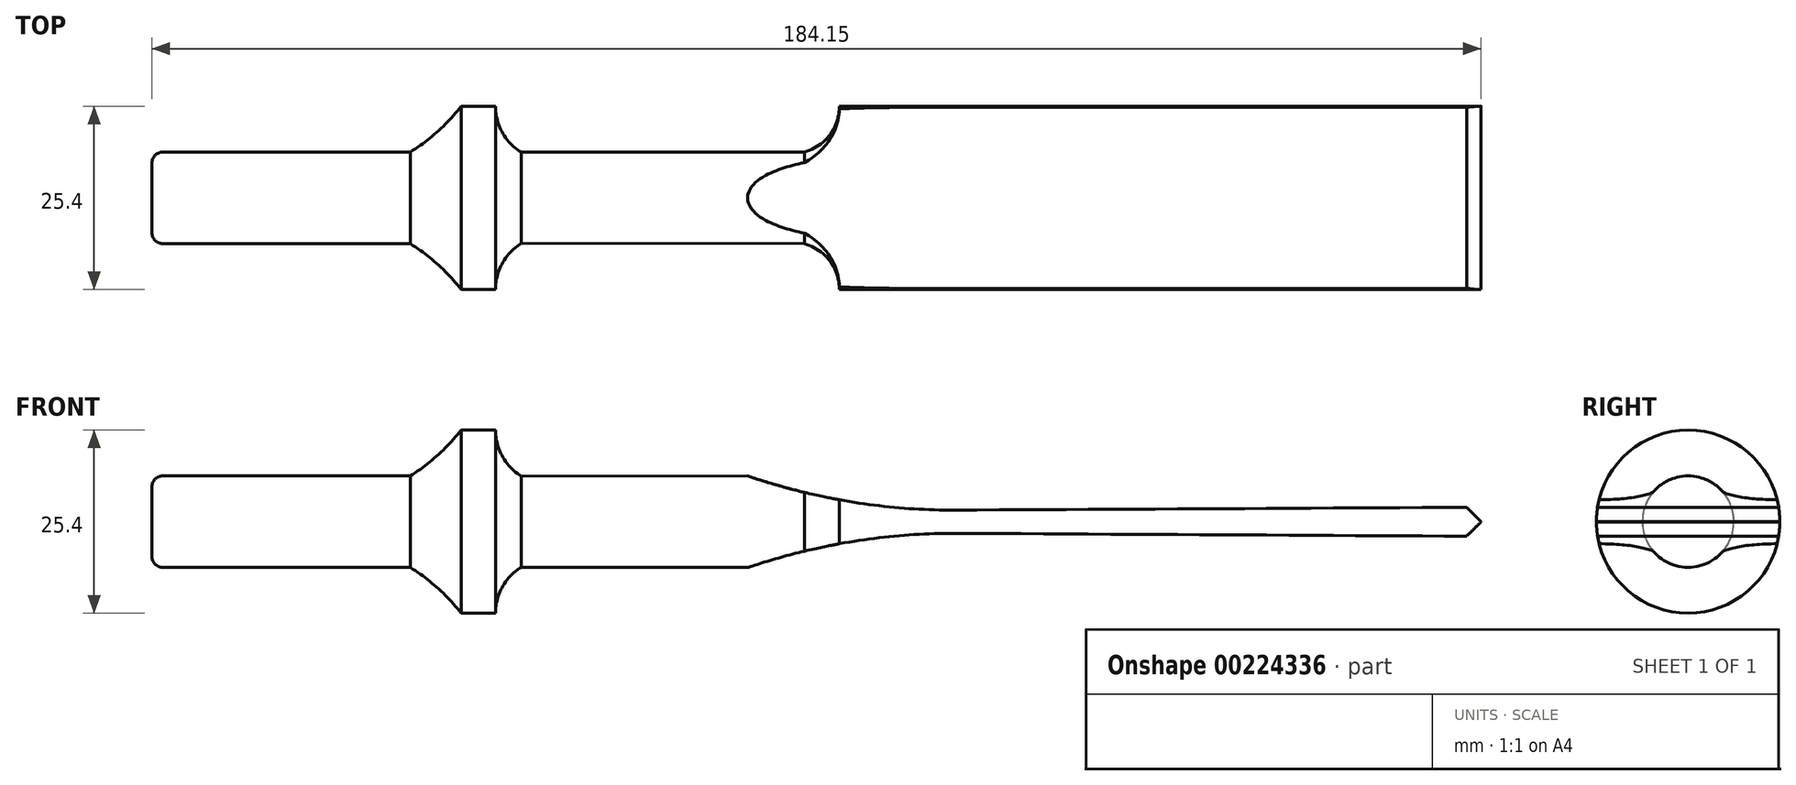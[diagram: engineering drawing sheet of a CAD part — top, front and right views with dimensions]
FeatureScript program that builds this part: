
annotation { "Feature Type Name" : "Feature", "Feature Type Description" : "" }
export const myFeature = defineFeature(function(context is Context, id is Id, definition is map)
    precondition{}
    {
        {
            var Q0;
            Q0=qCreatedBy(makeId("Front.planeOp"),FACE);
            var sketch = newSketch(context, id + "F0", { "sketchPlane" : qUnion([Q0])});
            skLineSegment(sketch, "E0", {"start": v(-87.11, -21.44) * mm, "end": v(95.51, -21.44) * mm});
            skLineSegment(sketch, "E1", {"start": v(95.51, -21.44) * mm, "end": v(95.51, -8.74) * mm});
            skLineSegment(sketch, "E2", {"start": v(-88.64, -19.91) * mm, "end": v(-88.64, -16.61) * mm});
            skLineSegment(sketch, "E3", {"start": v(-87.11, -15.09) * mm, "end": v(-52.84, -15.09) * mm});
            skLineSegment(sketch, "E4", {"start": v(95.51, -8.74) * mm, "end": v(6.61, -8.74) * mm});
            skLineSegment(sketch, "E5", {"start": v(-45.79, -8.74) * mm, "end": v(-41.04, -8.74) * mm});
            skLineSegment(sketch, "E6", {"start": v(-37.44, -15.12) * mm, "end": v(1.76, -15.1) * mm});
            skArc(sketch, "E7", {"start": v(-1.7, -15.1) * mm, "mid": v(4.03, -13.97) * mm, "end": v(6.61, -8.74) * mm});
            skArc(sketch, "E8", {"start": v(-41.04, -8.74) * mm, "mid": v(-40.08, -12.4) * mm, "end": v(-37.44, -15.12) * mm});
            skArc(sketch, "E9", {"start": v(-52.84, -15.09) * mm, "mid": v(-49.04, -12.22) * mm, "end": v(-45.79, -8.74) * mm});
            skPoint(sketch, "E10.visualSharp", {"position": v(-88.64, -15.09) * mm});
            skArc(sketch, "E10.filletArc", {"start": v(-87.11, -15.09) * mm, "mid": v(-88.2, -15.53) * mm, "end": v(-88.64, -16.61) * mm});
            skPoint(sketch, "E11.visualSharp", {"position": v(-88.64, -21.44) * mm});
            skArc(sketch, "E11.filletArc", {"start": v(-88.64, -19.91) * mm, "mid": v(-88.2, -21) * mm, "end": v(-87.11, -21.44) * mm});
            skSolve(sketch);
        }
        {
            var Q0;
            Q0 = qSketchRegion(id + "F0", true);
            var Q1;
            Q1=sQuery(id+"F0.wireOp",EDGE,"E0");
            revolve(context, id + "F1", {"entities" : qUnion([Q0]), "axis" : qUnion([Q1]), "revolveType" : RevolveType.FULL});
        }
        {
            var Q0;
            Q0=qCreatedBy(makeId("Front.planeOp"),FACE);
            var sketch = newSketch(context, id + "F2", { "sketchPlane" : qUnion([Q0])});
            skLineSegment(sketch, "E12", {"start": v(95.53, -8.76) * mm, "end": v(95.53, -34.16) * mm});
            skLineSegment(sketch, "E13", {"start": v(95.53, -21.46) * mm, "end": v(-108.1, -21.46) * mm, "construction": true});
            skLineSegment(sketch, "E14", {"start": v(95.53, -19.46) * mm, "end": v(95.53, -19.44) * mm, "construction": true});
            skLineSegment(sketch, "E15.0", {"start": v(-6.07, -8.75) * mm, "end": v(-6.07, -34.15) * mm, "construction": true});
            skLineSegment(sketch, "E16.0", {"start": v(95.46, -15.1) * mm, "end": v(-108.1, -15.1) * mm, "construction": true});
            skArc(sketch, "E17", {"start": v(-6.07, -15.1) * mm, "mid": v(8.05, -18.66) * mm, "end": v(22.57, -19.85) * mm});
            skPoint(sketch, "E18", {"position": v(-6.07, -15.1) * mm});
            skLineSegment(sketch, "E19", {"start": v(22.57, -19.85) * mm, "end": v(93.53, -19.46) * mm});
            skLineSegment(sketch, "E20", {"start": v(95.53, -21.46) * mm, "end": v(93.53, -19.46) * mm});
            skLineSegment(sketch, "E21", {"start": v(-6.07, -15.1) * mm, "end": v(-6.07, -5.35) * mm});
            skLineSegment(sketch, "E22", {"start": v(-6.07, -5.35) * mm, "end": v(95.46, -5.35) * mm});
            skLineSegment(sketch, "E23", {"start": v(95.46, -5.35) * mm, "end": v(105.15, -5.35) * mm});
            skLineSegment(sketch, "E24", {"start": v(105.15, -5.35) * mm, "end": v(105.15, -19.32) * mm});
            skLineSegment(sketch, "E25", {"start": v(105.15, -19.32) * mm, "end": v(95.53, -21.46) * mm});
            skPoint(sketch, "E26.trimOffspring.end.orphan", {"position": v(100.56, -19.44) * mm});
            skLineSegment(sketch, "E27.MirrorCS", {"start": v(-6.07, -34.16) * mm, "end": v(-6.07, -8.76) * mm, "construction": true});
            skLineSegment(sketch, "E28.MirrorCS", {"start": v(-6.07, -37.56) * mm, "end": v(95.46, -37.56) * mm});
            skArc(sketch, "E29.MirrorCS", {"start": v(-6.07, -27.8) * mm, "mid": v(8.05, -24.26) * mm, "end": v(22.57, -23.07) * mm});
            skLineSegment(sketch, "E30.MirrorCS", {"start": v(22.57, -23.07) * mm, "end": v(93.53, -23.46) * mm});
            skLineSegment(sketch, "E31.MirrorCS", {"start": v(95.53, -21.46) * mm, "end": v(93.53, -23.46) * mm});
            skLineSegment(sketch, "E32.MirrorCS", {"start": v(105.15, -23.6) * mm, "end": v(95.53, -21.46) * mm});
            skLineSegment(sketch, "E33.MirrorCS", {"start": v(105.15, -37.56) * mm, "end": v(105.15, -23.6) * mm});
            skLineSegment(sketch, "E34.MirrorCS", {"start": v(95.46, -37.56) * mm, "end": v(105.15, -37.56) * mm});
            skLineSegment(sketch, "E35.MirrorCS", {"start": v(-6.07, -27.8) * mm, "end": v(-6.07, -37.56) * mm});
            skSolve(sketch);
        }
        {
            var Q0;
            Q0=makeQuery(id+"F2.imprint","IMPRINT",FACE,{"disambiguationData":[TD([[makeQuery(id+"F2.imprint","IMPRINT",EDGE,{"derivedFrom":sQuery(id+"F2.wireOp",EDGE,"E17")}),1.0]])]});
            var Q1;
            Q1=makeQuery(id+"F2.imprint","IMPRINT",FACE,{"disambiguationData":[TD([[makeQuery(id+"F2.imprint","IMPRINT",EDGE,{"derivedFrom":sQuery(id+"F2.wireOp",EDGE,"E28.MirrorCS")}),1.0]])]});
            extrude(context, id + "F3", {"entities" : qUnion([Q0, Q1]), "operationType" : NewBodyOperationType.REMOVE, "oppositeDirection" : true, "depth" : 25.4 * mm});
        }
        {
            var Q0;
            Q0 = qSketchRegion(id + "F2", true);
            extrude(context, id + "F4", {"entities" : qUnion([Q0]), "operationType" : NewBodyOperationType.REMOVE, "depth" : 25.4 * mm});
        }
    });
